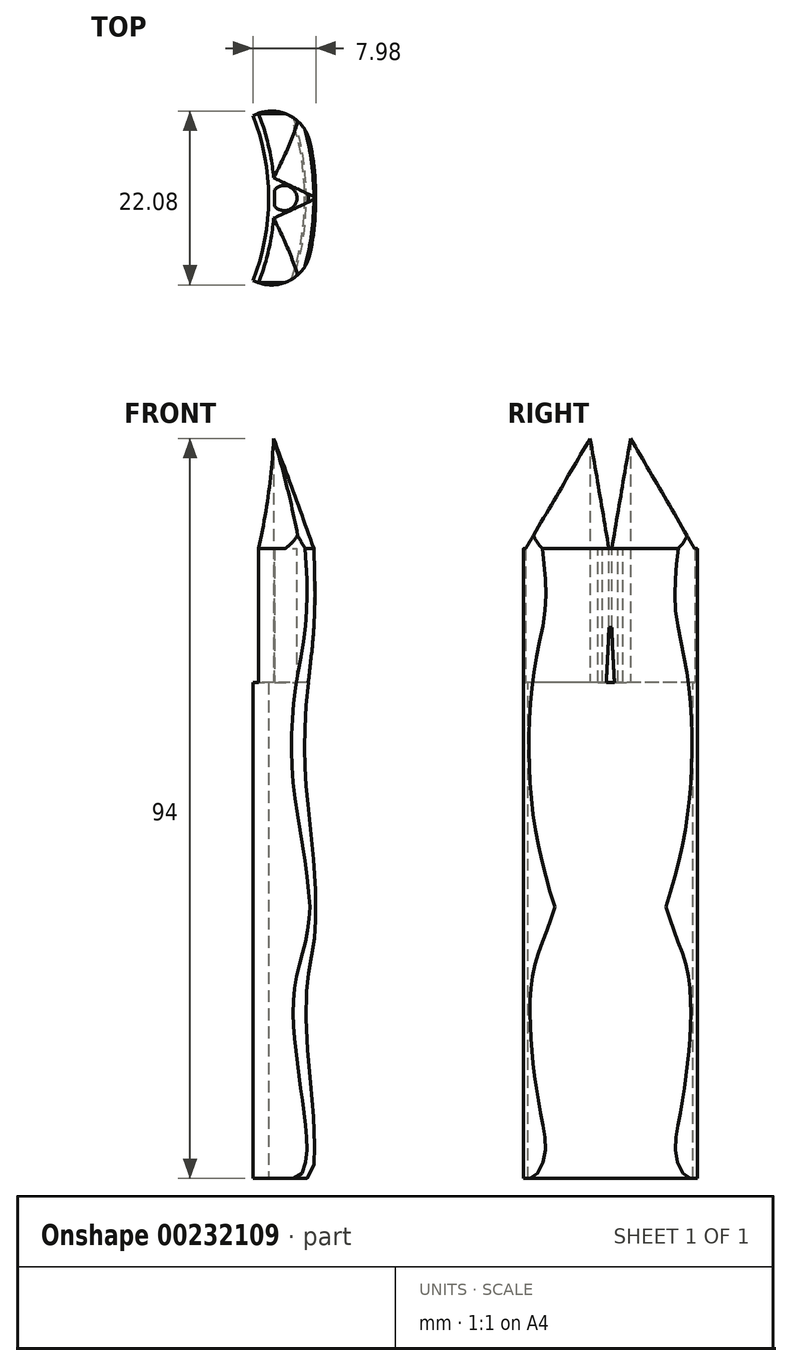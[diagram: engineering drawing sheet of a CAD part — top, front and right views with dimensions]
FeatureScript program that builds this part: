
annotation { "Feature Type Name" : "Feature", "Feature Type Description" : "" }
export const myFeature = defineFeature(function(context is Context, id is Id, definition is map)
    precondition{}
    {
        {
            var Q0;
            Q0=qCreatedBy(makeId("Front.planeOp"),FACE);
            var sketch = newSketch(context, id + "F0", { "sketchPlane" : qUnion([Q0])});
            skLineSegment(sketch, "E0", {"start": v(0, 0) * mm, "end": v(-28.6, 0) * mm, "construction": true});
            skLineSegment(sketch, "E1", {"start": v(-28.6, 0) * mm, "end": v(-28.6, 10) * mm, "construction": true});
            skLineSegment(sketch, "E2", {"start": v(0, 0) * mm, "end": v(4.75, 0) * mm});
            skLineSegment(sketch, "E3", {"start": v(0, 0) * mm, "end": v(0, 63) * mm});
            skLineSegment(sketch, "E4", {"start": v(0, 63) * mm, "end": v(0.75, 63) * mm});
            skLineSegment(sketch, "E5", {"start": v(0.75, 63) * mm, "end": v(0.75, 80) * mm});
            skLineSegment(sketch, "E6", {"start": v(5.75, 80) * mm, "end": v(5.75, 60) * mm, "construction": true});
            skLineSegment(sketch, "E7", {"start": v(5.75, 60) * mm, "end": v(4.75, 60) * mm, "construction": true});
            skLineSegment(sketch, "E8", {"start": v(4.75, 60) * mm, "end": v(4.75, 40) * mm, "construction": true});
            skLineSegment(sketch, "E9", {"start": v(4.75, 40) * mm, "end": v(5.75, 40) * mm, "construction": true});
            skLineSegment(sketch, "E10", {"start": v(5.75, 40) * mm, "end": v(5.75, 20) * mm, "construction": true});
            skLineSegment(sketch, "E11", {"start": v(5.75, 20) * mm, "end": v(4.75, 20) * mm, "construction": true});
            skFitSpline(sketch, "E12", {"points": [v(5.75, 80) * mm, v(5.75, 70) * mm, v(4.75, 60) * mm, v(4.75, 50) * mm, v(5.75, 40) * mm, v(5.75, 30) * mm, v(4.75, 20) * mm, v(4.75, 0) * mm], "startDerivative": vector(2.34, -74.3) * mm, "endDerivative": vector(-37.4, 0.16) * mm});
            skLineSegment(sketch, "E13", {"start": v(4.75, 0) * mm, "end": v(5.75, 0) * mm});
            skLineSegment(sketch, "E14", {"start": v(0.75, 80) * mm, "end": v(0.75, 94) * mm});
            skLineSegment(sketch, "E15", {"start": v(0.75, 94) * mm, "end": v(5.75, 80) * mm});
            skSolve(sketch);
        }
        {
            var Q0;
            Q0 = qSketchRegion(id + "F0", true);
            var Q1;
            Q1 = qConstructionFilter(qBodyType(qCreatedBy(id + "F0" ,EDGE), BodyType.WIRE), ConstructionObject.NO);
            var Q2;
            Q2=sQuery(id+"F0.wireOp",EDGE,"E1");
            revolve(context, id + "F1", {"entities" : qUnion([Q0]), "surfaceEntities" : qUnion([Q1]), "axis" : qUnion([Q2]), "revolveType" : RevolveType.SYMMETRIC, "angle" : 43 * degree});
        }
        {
            var Q0;
            Q0=qCreatedBy(makeId("Top.planeOp"),FACE);
            cPlane(context, id + "F2", {"entities" : qUnion([Q0]), "cplaneType" : CPlaneType.OFFSET, "offset" : 80 * mm, "width" : 150 * mm, "height" : 150 * mm});
        }
        {
            var Q0;
            Q0=qCreatedBy(id+"F2.planeOp",FACE);
            var sketch = newSketch(context, id + "F3", { "sketchPlane" : qUnion([Q0])});
            skLineSegment(sketch, "E16", {"start": v(0, 0) * mm, "end": v(6.15, 0) * mm, "construction": true});
            skLineSegment(sketch, "E17", {"start": v(6.15, 0) * mm, "end": v(0.64, 2.57) * mm});
            skLineSegment(sketch, "E18", {"start": v(6.15, 0) * mm, "end": v(0.64, -2.57) * mm});
            skArc(sketch, "E19.0.0", {"start": v(0.64, 2.57) * mm, "mid": v(0.75, 0) * mm, "end": v(0.64, -2.57) * mm});
            skArc(sketch, "E19.0.2", {"start": v(5.75, -0.19) * mm, "mid": v(5.75, 0) * mm, "end": v(5.75, 0.19) * mm});
            skPoint(sketch, "E20.orphan", {"position": v(3.36, 12.6) * mm});
            skPoint(sketch, "E21.orphan", {"position": v(-1.3, 10.76) * mm});
            skPoint(sketch, "E19.0.1.start.orphan", {"position": v(-1.3, -10.76) * mm});
            skPoint(sketch, "E22.orphan", {"position": v(3.36, -12.6) * mm});
            skLineSegment(sketch, "E23", {"start": v(0, 0) * mm, "end": v(2, 0) * mm, "construction": true});
            skCircle(sketch, "E24", {"center": v(2, 0) * mm, "radius": 1.6 * mm});
            skSolve(sketch);
        }
        {
            var Q0;
            Q0 = qSketchRegion(id + "F3", true);
            extrude(context, id + "F4", {"entities" : qUnion([Q0]), "operationType" : NewBodyOperationType.REMOVE, "depth" : 25 * mm});
        }
        {
            var Q0;
            {var subQ0=sQuery(id+"F3.wireOp",EDGE,"E24");var subQ1=sQuery(id+"F3.wireOp",EDGE,"E19.0.0");var subQ2=makeQuery(id+"F3.imprint","INTERSECT",VERTEX,{"disambiguationData":[OD(0.0)],"derivedFrom":[subQ1,subQ0]});Q0=makeQuery(id+"F3.imprint","IMPRINT",FACE,{"disambiguationData":[TD([[makeQuery(id+"F3.imprint","IMPRINT",EDGE,{"disambiguationData":[TD([[subQ2,-1.0]])],"derivedFrom":subQ1}),1.0]])]});}
            var Q1;
            {var subQ0=sQuery(id+"F3.wireOp",EDGE,"E24");var subQ1=sQuery(id+"F3.wireOp",EDGE,"E19.0.0");var subQ2=makeQuery(id+"F3.imprint","INTERSECT",VERTEX,{"disambiguationData":[OD(0.0)],"derivedFrom":[subQ1,subQ0]});Q1=makeQuery(id+"F3.imprint","IMPRINT",FACE,{"disambiguationData":[TD([[makeQuery(id+"F3.imprint","IMPRINT",EDGE,{"disambiguationData":[TD([[subQ2,-1.0]])],"derivedFrom":subQ1}),-1.0]])]});}
            extrude(context, id + "F5", {"entities" : qUnion([Q0, Q1]), "operationType" : NewBodyOperationType.REMOVE, "oppositeDirection" : true, "depth" : 17 * mm});
        }
        {
            var Q0;
            Q0=makeQuery(id+"F1.opRevolve","SWEPT_FACE",FACE,{"disambiguationData":[OSD([sQuery(id+"F0.wireOp",EDGE,"E2")])]});
            var sketch = newSketch(context, id + "F6", { "sketchPlane" : qUnion([Q0])});
            skLineSegment(sketch, "E25.0.1", {"start": v(-1.47, 10.7) * mm, "end": v(-2, 10.49) * mm});
            skLineSegment(sketch, "E25.0.3", {"start": v(-2, -10.49) * mm, "end": v(-1.47, -10.7) * mm});
            skPoint(sketch, "E26.newPointA", {"position": v(2.43, 12.23) * mm});
            skArc(sketch, "E26.filletArc", {"start": v(5.26, 7.06) * mm, "mid": v(2.74, 10.44) * mm, "end": v(-1.47, 10.7) * mm});
            skPoint(sketch, "E27.newPointB", {"position": v(2.43, -12.23) * mm});
            skArc(sketch, "E27.filletArc", {"start": v(-1.47, -10.7) * mm, "mid": v(2.74, -10.44) * mm, "end": v(5.26, -7.06) * mm});
            skLineSegment(sketch, "E28.0.1", {"start": v(2.43, 12.23) * mm, "end": v(-2, 10.49) * mm});
            skLineSegment(sketch, "E28.0.3", {"start": v(-2, -10.49) * mm, "end": v(2.43, -12.23) * mm});
            skArc(sketch, "E29", {"start": v(3.58, -12.68) * mm, "mid": v(4.54, -9.9) * mm, "end": v(5.26, -7.06) * mm});
            skArc(sketch, "E30.trimOffspring", {"start": v(5.26, 7.06) * mm, "mid": v(4.54, 9.9) * mm, "end": v(3.58, 12.68) * mm});
            skLineSegment(sketch, "E31", {"start": v(3.58, 12.68) * mm, "end": v(-2, 10.49) * mm});
            skLineSegment(sketch, "E32", {"start": v(-2, -10.49) * mm, "end": v(3.58, -12.68) * mm});
            skSolve(sketch);
        }
        {
            var Q0;
            Q0 = qSketchRegion(id + "F6", true);
            extrude(context, id + "F7", {"entities" : qUnion([Q0]), "operationType" : NewBodyOperationType.REMOVE, "endBound" : BoundingType.THROUGH_ALL, "oppositeDirection" : true, "depth" : 25 * mm});
        }
        {
            var Q0;
            Q0=qCreatedBy(makeId("Right.planeOp"),FACE);
            var sketch = newSketch(context, id + "F8", { "sketchPlane" : qUnion([Q0])});
            skLineSegment(sketch, "E33.0.0", {"start": v(-10.76, 63) * mm, "end": v(-10.76, 80) * mm, "construction": true});
            skLineSegment(sketch, "E33.0.3", {"start": v(-2.57, 80) * mm, "end": v(-0.98, 80) * mm, "construction": true});
            skLineSegment(sketch, "E33.0.4", {"start": v(-0.98, 80) * mm, "end": v(-0.98, 63) * mm, "construction": true});
            skLineSegment(sketch, "E33.0.5", {"start": v(-0.98, 63) * mm, "end": v(-10.76, 63) * mm, "construction": true});
            skLineSegment(sketch, "E34", {"start": v(-2.57, 80) * mm, "end": v(-10.76, 80) * mm, "construction": true});
            skLineSegment(sketch, "E35", {"start": v(-2.57, 80) * mm, "end": v(2.57, 80) * mm, "construction": true});
            skLineSegment(sketch, "E36.0.1", {"start": v(10.76, 63) * mm, "end": v(0.98, 63) * mm, "construction": true});
            skLineSegment(sketch, "E36.0.2", {"start": v(0.98, 63) * mm, "end": v(0.98, 80) * mm, "construction": true});
            skLineSegment(sketch, "E36.0.3", {"start": v(0.98, 80) * mm, "end": v(2.57, 80) * mm, "construction": true});
            skLineSegment(sketch, "E37", {"start": v(-10.76, 80) * mm, "end": v(-12.22, 80) * mm});
            skLineSegment(sketch, "E38", {"start": v(-12.22, 80) * mm, "end": v(-12.22, 95.2) * mm});
            skLineSegment(sketch, "E39", {"start": v(-12.22, 95.2) * mm, "end": v(-2.82, 95.2) * mm});
            skLineSegment(sketch, "E40", {"start": v(-2.82, 95.2) * mm, "end": v(-2.57, 94) * mm});
            skPoint(sketch, "E41.end.orphan", {"position": v(10.76, 94) * mm});
            skLineSegment(sketch, "E42", {"start": v(10.7, 80) * mm, "end": v(13.5, 80) * mm});
            skLineSegment(sketch, "E43", {"start": v(13.5, 80) * mm, "end": v(12.39, 95.32) * mm});
            skLineSegment(sketch, "E44", {"start": v(12.39, 95.32) * mm, "end": v(2.02, 94.56) * mm});
            skLineSegment(sketch, "E45", {"start": v(2.02, 94.56) * mm, "end": v(2.57, 94) * mm});
            skPoint(sketch, "E46.end.orphan", {"position": v(-10.76, 94) * mm});
            skLineSegment(sketch, "E47", {"start": v(-2.57, 94) * mm, "end": v(-10.76, 80) * mm});
            skLineSegment(sketch, "E48", {"start": v(2.57, 94) * mm, "end": v(10.7, 80) * mm});
            skSolve(sketch);
        }
        {
            var Q0;
            Q0 = qSketchRegion(id + "F8", true);
            extrude(context, id + "F9", {"entities" : qUnion([Q0]), "operationType" : NewBodyOperationType.REMOVE, "endBound" : BoundingType.SYMMETRIC, "oppositeDirection" : true, "depth" : 25 * mm});
        }
    });
